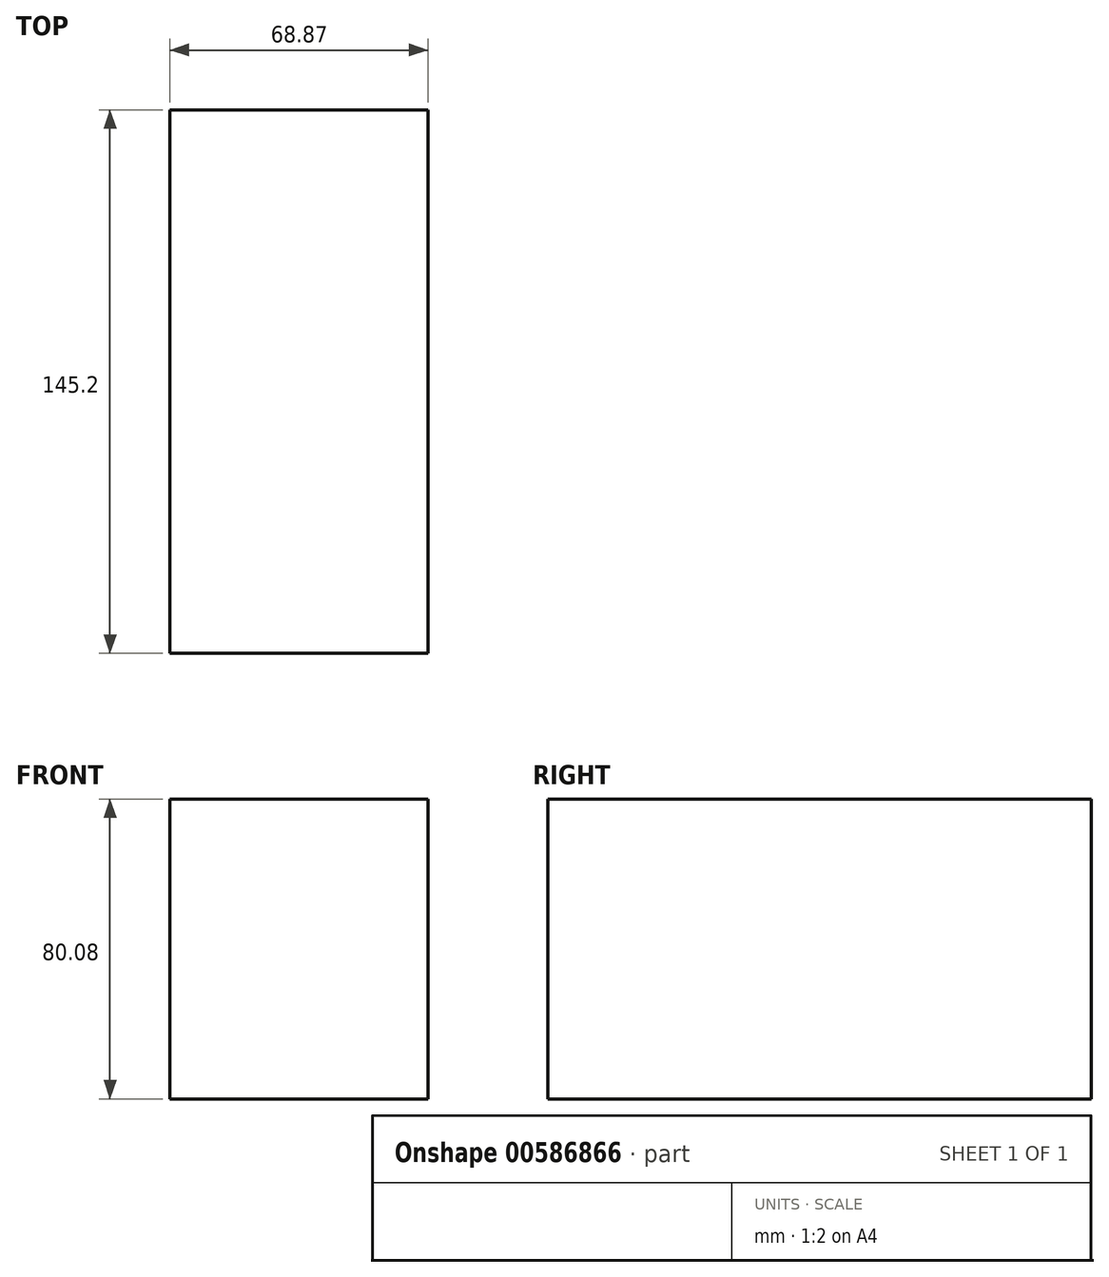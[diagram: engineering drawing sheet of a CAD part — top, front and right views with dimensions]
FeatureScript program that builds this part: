
annotation { "Feature Type Name" : "Feature", "Feature Type Description" : "" }
export const myFeature = defineFeature(function(context is Context, id is Id, definition is map)
    precondition{}
    {
        {
            var Q0;
            Q0=qCreatedBy(makeId("Front.planeOp"),FACE);
            var sketch = newSketch(context, id + "F0", { "sketchPlane" : qUnion([Q0])});
            skLineSegment(sketch, "E0", {"start": v(42.38, 49.94) * mm, "end": v(42.38, 49.94) * mm});
            skLineSegment(sketch, "E1", {"start": v(42.38, 49.94) * mm, "end": v(-26.5, 49.94) * mm});
            skLineSegment(sketch, "E2", {"start": v(-26.5, 49.94) * mm, "end": v(-26.5, -30.14) * mm});
            skLineSegment(sketch, "E3", {"start": v(-26.5, -30.14) * mm, "end": v(42.38, -30.14) * mm});
            skLineSegment(sketch, "E4", {"start": v(42.38, -30.14) * mm, "end": v(42.38, 49.94) * mm});
            skLineSegment(sketch, "E5", {"start": v(42.38, 49.94) * mm, "end": v(70.94, 49.94) * mm});
            skLineSegment(sketch, "E6", {"start": v(70.94, 49.94) * mm, "end": v(70.94, 16.95) * mm});
            skLineSegment(sketch, "E7", {"start": v(70.94, 16.95) * mm, "end": v(42.38, 9.9) * mm});
            skLineSegment(sketch, "E8.0", {"start": v(-32.84, 49.94) * mm, "end": v(-32.84, -30.14) * mm});
            skSolve(sketch);
        }
        {
            var Q0;
            {var subQ3=sQuery(id+"F0.wireOp",EDGE,"E1");Q0=makeQuery(id+"F0.imprint","IMPRINT",FACE,{"disambiguationData":[TD([[makeQuery(id+"F0.imprint","IMPRINT",EDGE,{"derivedFrom":subQ3}),1.0]])]});}
            extrude(context, id + "F1", {"entities" : qUnion([Q0]), "depth" : 145.2 * mm, "offsetDistance" : 25.4 * mm});
        }
    });
